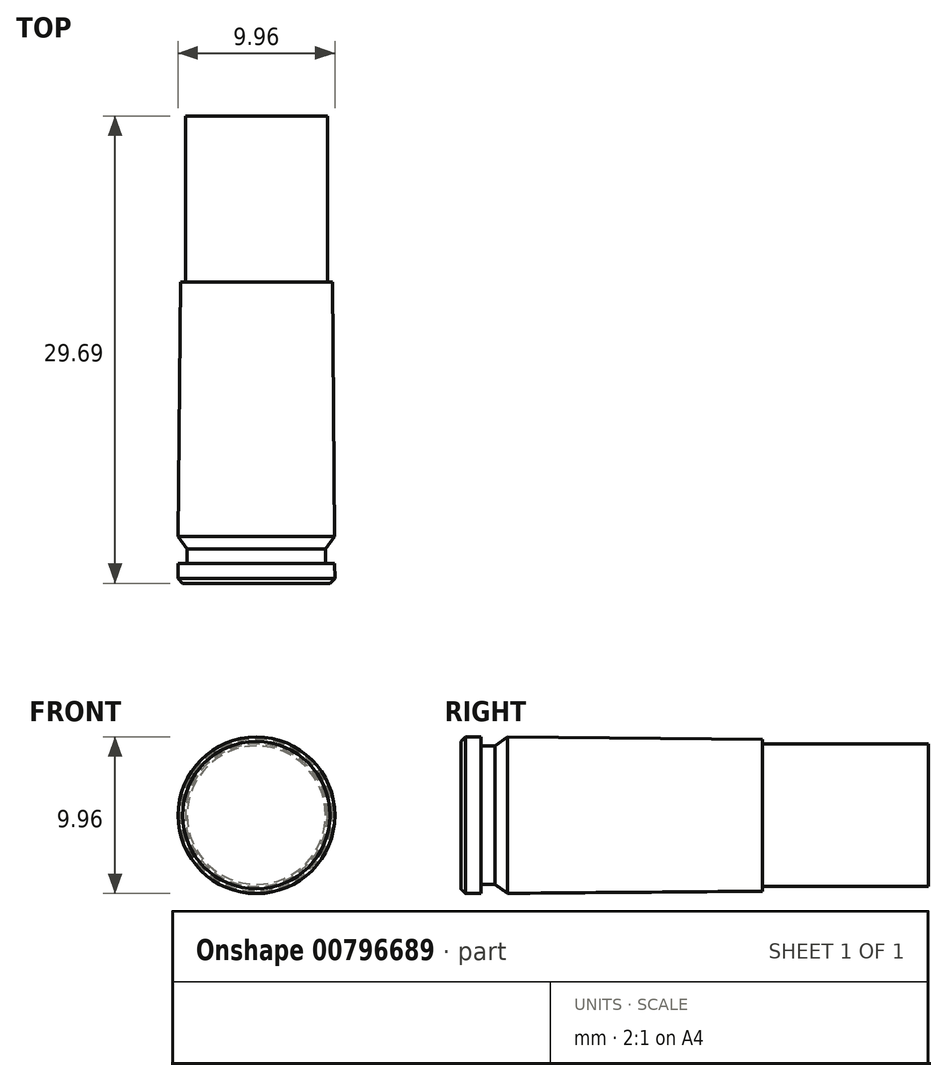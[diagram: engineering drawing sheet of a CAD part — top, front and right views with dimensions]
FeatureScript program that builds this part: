
annotation { "Feature Type Name" : "Feature", "Feature Type Description" : "" }
export const myFeature = defineFeature(function(context is Context, id is Id, definition is map)
    precondition{}
    {
        {
            var Q0;
            Q0=qCreatedBy(makeId("Right.planeOp"),FACE);
            var sketch = newSketch(context, id + "F0", { "sketchPlane" : qUnion([Q0])});
            skLineSegment(sketch, "E0", {"start": v(0, 0) * mm, "end": v(0.3, 0) * mm});
            skLineSegment(sketch, "E1", {"start": v(0, -2.44) * mm, "end": v(1.27, -2.44) * mm});
            skLineSegment(sketch, "E2", {"start": v(0.3, 0) * mm, "end": v(1.27, 0) * mm});
            skLineSegment(sketch, "E3", {"start": v(1.27, 0) * mm, "end": v(2.17, 0) * mm});
            skLineSegment(sketch, "E4", {"start": v(0, -4.03) * mm, "end": v(2.98, -4.03) * mm});
            skLineSegment(sketch, "E5", {"start": v(0, -6.4) * mm, "end": v(19.15, -6.4) * mm});
            skLineSegment(sketch, "E6", {"start": v(0, -10.9) * mm, "end": v(29.7, -10.9) * mm});
            skLineSegment(sketch, "E7", {"start": v(2.17, 0) * mm, "end": v(2.98, 0) * mm});
            skLineSegment(sketch, "E8", {"start": v(2.98, 0) * mm, "end": v(19.15, 0) * mm});
            skLineSegment(sketch, "E9", {"start": v(19.15, 0) * mm, "end": v(29.7, 0) * mm});
            skLineSegment(sketch, "E10", {"start": v(29.7, 0) * mm, "end": v(29.7, 4.51) * mm});
            skLineSegment(sketch, "E11", {"start": v(29.7, 4.51) * mm, "end": v(19.15, 4.51) * mm});
            skLineSegment(sketch, "E12", {"start": v(19.15, 0) * mm, "end": v(19.15, 4.83) * mm});
            skLineSegment(sketch, "E13", {"start": v(19.15, 4.82) * mm, "end": v(2.98, 4.96) * mm});
            skLineSegment(sketch, "E14", {"start": v(2.98, 0) * mm, "end": v(2.98, 4.96) * mm});
            skLineSegment(sketch, "E15", {"start": v(2.17, 0) * mm, "end": v(2.17, 4.4) * mm});
            skLineSegment(sketch, "E16", {"start": v(2.17, 4.4) * mm, "end": v(2.98, 4.96) * mm});
            skLineSegment(sketch, "E17", {"start": v(0.3, 0) * mm, "end": v(0.3, 4.98) * mm});
            skLineSegment(sketch, "E18", {"start": v(0.3, 4.98) * mm, "end": v(1.27, 4.96) * mm});
            skLineSegment(sketch, "E19", {"start": v(1.27, 4.96) * mm, "end": v(1.27, 4.4) * mm});
            skLineSegment(sketch, "E20", {"start": v(1.27, 4.4) * mm, "end": v(2.17, 4.4) * mm});
            skLineSegment(sketch, "E21", {"start": v(0, 0) * mm, "end": v(0, 4.68) * mm});
            skLineSegment(sketch, "E22", {"start": v(0, 4.68) * mm, "end": v(0.3, 4.98) * mm});
            skLineSegment(sketch, "E23", {"start": v(-0.07, 4.98) * mm, "end": v(0.3, 4.98) * mm});
            skSolve(sketch);
        }
        {
            var Q0;
            Q0=makeQuery(id+"F0.imprint","IMPRINT",FACE,{"disambiguationData":[TD([[makeQuery(id+"F0.imprint","IMPRINT",EDGE,{"derivedFrom":sQuery(id+"F0.wireOp",EDGE,"E0")}),1.0]])]});
            var Q1;
            Q1=makeQuery(id+"F0.imprint","IMPRINT",FACE,{"disambiguationData":[TD([[makeQuery(id+"F0.imprint","IMPRINT",EDGE,{"derivedFrom":sQuery(id+"F0.wireOp",EDGE,"E2")}),1.0]])]});
            var Q2;
            Q2=makeQuery(id+"F0.imprint","IMPRINT",FACE,{"disambiguationData":[TD([[makeQuery(id+"F0.imprint","IMPRINT",EDGE,{"derivedFrom":sQuery(id+"F0.wireOp",EDGE,"E7")}),1.0]])]});
            var Q3;
            {var subQ2=sQuery(id+"F0.wireOp",EDGE,"E8");Q3=makeQuery(id+"F0.imprint","IMPRINT",FACE,{"disambiguationData":[TD([[makeQuery(id+"F0.imprint","IMPRINT",EDGE,{"derivedFrom":subQ2}),1.0]])]});}
            var Q4;
            {var subQ0=sQuery(id+"F0.wireOp",EDGE,"E9");Q4=makeQuery(id+"F0.imprint","IMPRINT",FACE,{"disambiguationData":[TD([[makeQuery(id+"F0.imprint","IMPRINT",EDGE,{"derivedFrom":subQ0}),1.0]])]});}
            var Q5;
            Q5=sQuery(id+"F0.wireOp",EDGE,"E8");
            revolve(context, id + "F1", {"surfaceOperationType" : NewSurfaceOperationType.NEW, "entities" : qUnion([Q0, Q1, Q2, Q3, Q4]), "axis" : qUnion([Q5]), "revolveType" : RevolveType.FULL});
        }
    });
